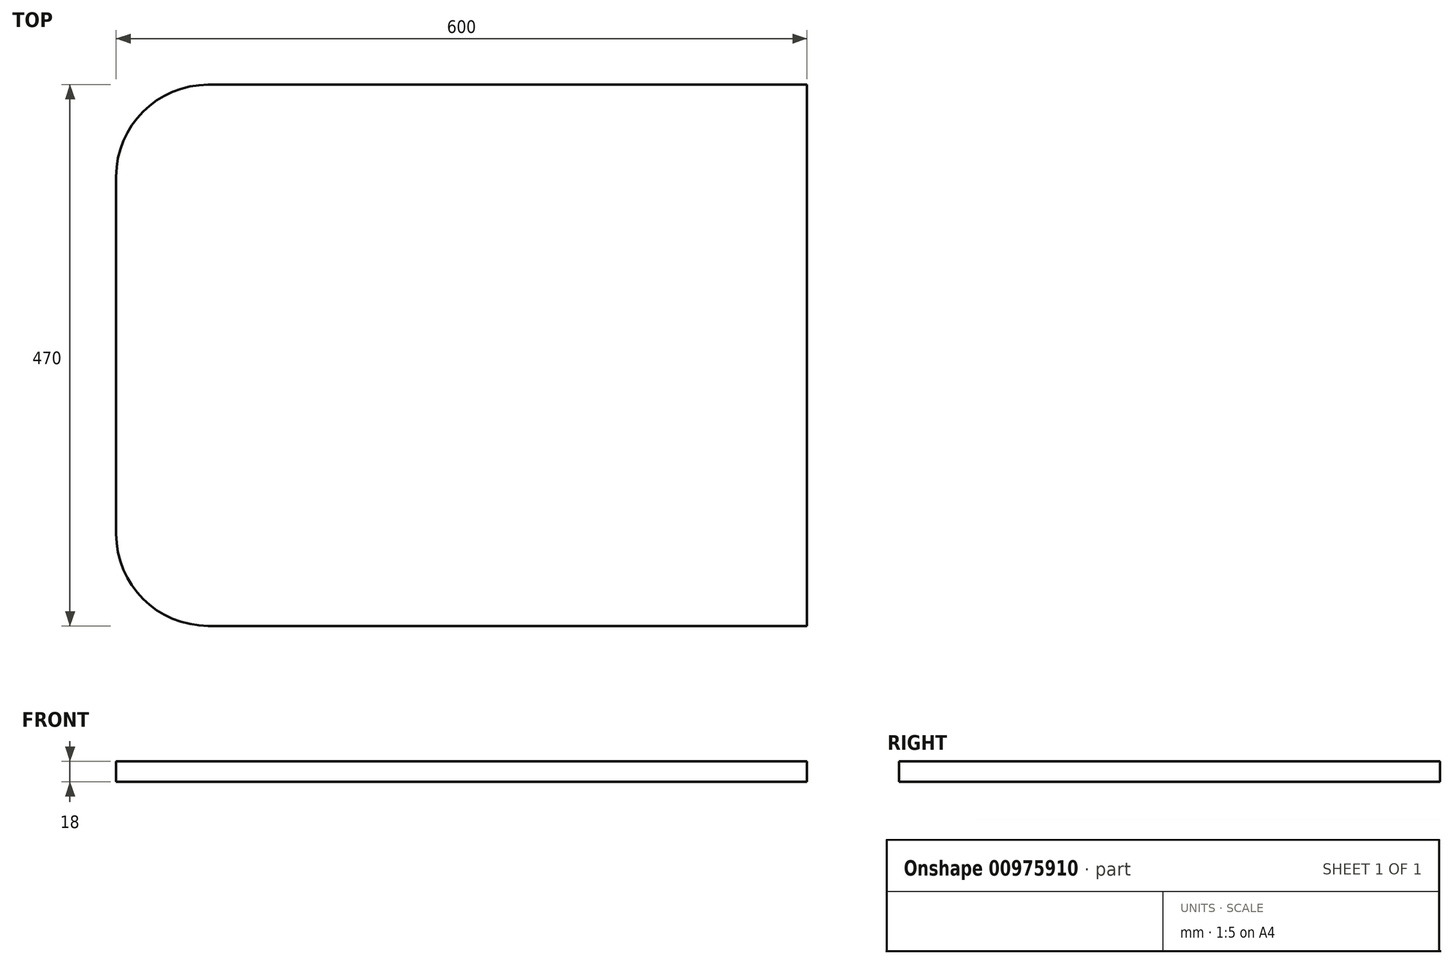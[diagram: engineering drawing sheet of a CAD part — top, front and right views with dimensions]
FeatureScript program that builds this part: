
annotation { "Feature Type Name" : "Feature", "Feature Type Description" : "" }
export const myFeature = defineFeature(function(context is Context, id is Id, definition is map)
    precondition{}
    {
        {
            var Q0;
            Q0=qCreatedBy(makeId("Top.planeOp"),FACE);
            var sketch = newSketch(context, id + "F0", { "sketchPlane" : qUnion([Q0])});
            skLineSegment(sketch, "E0.bottom", {"start": v(-463.55, 428.48) * mm, "end": v(56.45, 428.48) * mm});
            skLineSegment(sketch, "E0.top", {"start": v(-463.55, -41.52) * mm, "end": v(56.45, -41.52) * mm});
            skLineSegment(sketch, "E0.left", {"start": v(-543.55, 348.48) * mm, "end": v(-543.55, 38.48) * mm});
            skLineSegment(sketch, "E0.right", {"start": v(56.45, 428.48) * mm, "end": v(56.45, -41.52) * mm});
            skPoint(sketch, "E1.visualSharp", {"position": v(-543.55, 428.48) * mm});
            skArc(sketch, "E1.filletArc", {"start": v(-463.55, 428.48) * mm, "mid": v(-520.12, 405.05) * mm, "end": v(-543.55, 348.48) * mm});
            skPoint(sketch, "E2.visualSharp", {"position": v(-543.55, -41.52) * mm});
            skArc(sketch, "E2.filletArc", {"start": v(-543.55, 38.48) * mm, "mid": v(-520.12, -18.09) * mm, "end": v(-463.55, -41.52) * mm});
            skSolve(sketch);
        }
        {
            var Q0;
            Q0=makeQuery(id+"F0.imprint","IMPRINT",FACE,{"disambiguationData":[TD([[makeQuery(id+"F0.imprint","IMPRINT",EDGE,{"derivedFrom":sQuery(id+"F0.wireOp",EDGE,"E0.bottom")}),-1.0]])]});
            extrude(context, id + "F1", {"entities" : qUnion([Q0]), "depth" : 18 * mm, "offsetDistance" : 25 * mm});
        }
    });
